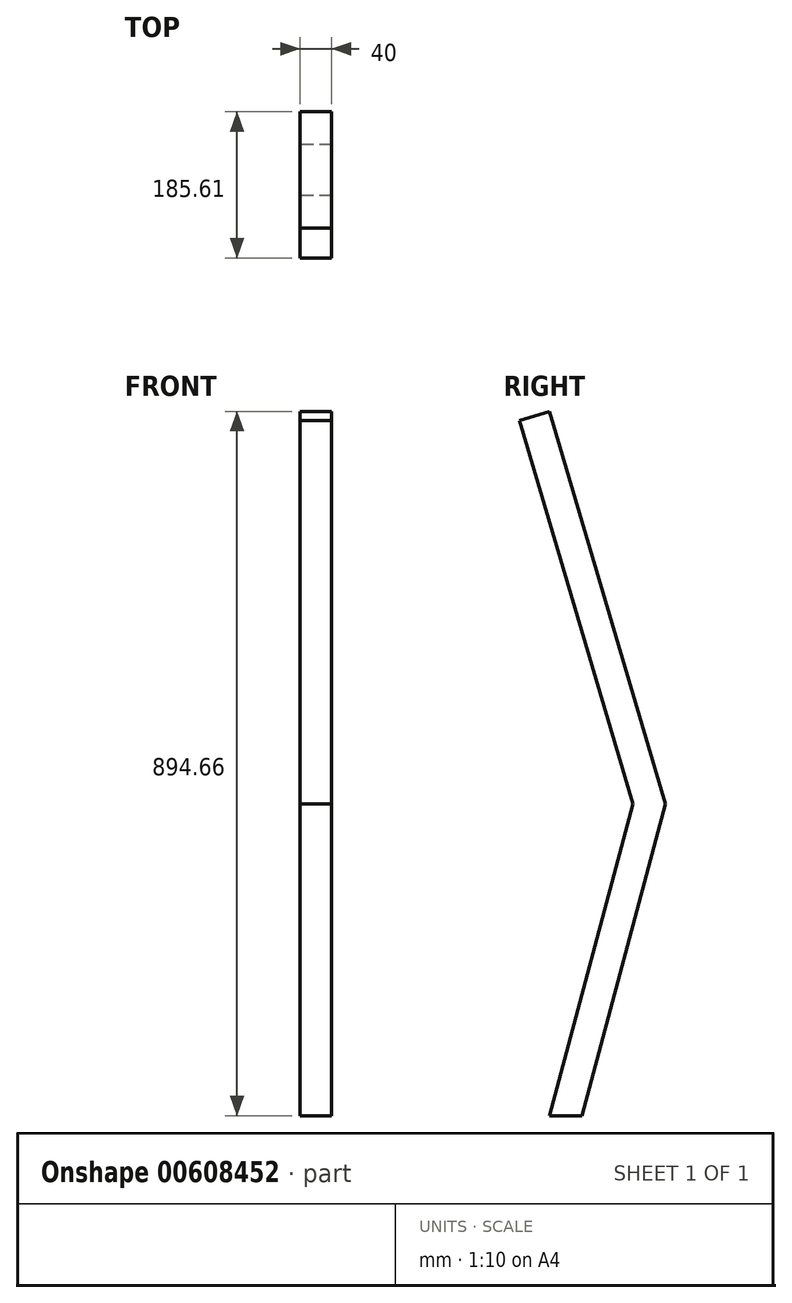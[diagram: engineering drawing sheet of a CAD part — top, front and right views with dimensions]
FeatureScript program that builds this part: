
annotation { "Feature Type Name" : "Feature", "Feature Type Description" : "" }
export const myFeature = defineFeature(function(context is Context, id is Id, definition is map)
    precondition{}
    {
        {
            var Q0;
            Q0=qCreatedBy(makeId("Right.planeOp"),FACE);
            var sketch = newSketch(context, id + "F0", { "sketchPlane" : qUnion([Q0])});
            skLineSegment(sketch, "E0", {"start": v(-307.1, 602.1) * mm, "end": v(-162.9, 114.74) * mm});
            skLineSegment(sketch, "E1", {"start": v(-162.9, 114.74) * mm, "end": v(-269.02, -281.3) * mm});
            skLineSegment(sketch, "E2", {"start": v(-269.02, -281.3) * mm, "end": v(-227.6, -281.3) * mm});
            skLineSegment(sketch, "E3", {"start": v(-227.6, -281.3) * mm, "end": v(-121.5, 114.74) * mm});
            skPoint(sketch, "E4.end.orphan", {"position": v(-142.12, 114.74) * mm});
            skLineSegment(sketch, "E5", {"start": v(-121.5, 114.74) * mm, "end": v(-269.02, 613.37) * mm});
            skLineSegment(sketch, "E6", {"start": v(-269.02, 613.37) * mm, "end": v(-307.1, 602.1) * mm});
            skPoint(sketch, "E7.orphan", {"position": v(-310.43, 613.37) * mm});
            skSolve(sketch);
        }
        {
            var Q0;
            Q0=makeQuery(id+"F0.imprint","IMPRINT",FACE,{"disambiguationData":[TD([[makeQuery(id+"F0.imprint","IMPRINT",EDGE,{"derivedFrom":sQuery(id+"F0.wireOp",EDGE,"E0")}),1.0]])]});
            extrude(context, id + "F1", {"entities" : qUnion([Q0]), "depth" : 40 * mm, "offsetDistance" : 25 * mm});
        }
    });
